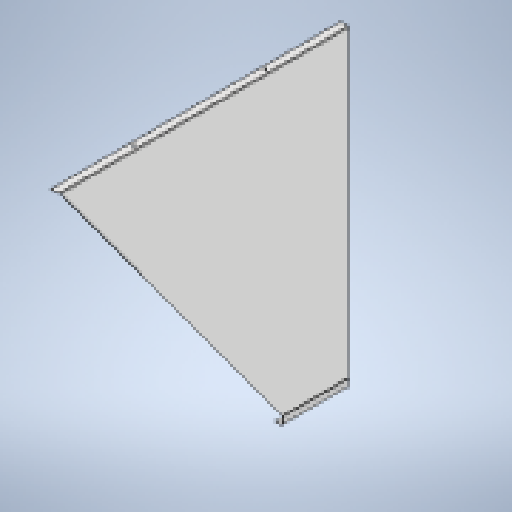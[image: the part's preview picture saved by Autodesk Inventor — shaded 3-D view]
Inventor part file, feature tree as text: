
AUTODESK INVENTOR PART (.ipt)
format: ipt  version: 2025.1 (Build 291241020, 241B)  size: 336,896 bytes
history: native  units: mm
features: sheet_metal_op x9, sketch x8, other x7, extrude x3, mirror x1, pattern_linear x1, projected_geometry x1
ambient origin geometry x8: Origin, YZ Plane, XZ Plane, XY Plane, X Axis, Y Axis, Z Axis, Center Point
bodies: Body1 (feature_tree)
feature tree (30):
  sheet_metal_op  "Contour Flange2"
  extrude  "Extrusion7"  Depth=8.0mm
  extrude  "Extrusion11"  Depth=3.0mm
  other  "A-Side Definition"
  extrude  "Extrusion15"  Depth=3.0mm
  mirror  "Mirror1"
  sheet_metal_op  "Flange3"
  sheet_metal_op  "Flange4"
  pattern_linear  "Rectangular Pattern1"  Count1=174  [1 undecoded]
  sketch  "Sketch1"  dims[d0=1170.0mm d63=8.0mm]
  other  "Plate4"
  sheet_metal_op  "Bend4"
  sheet_metal_op  "Corner4"
  sketch  "Sketch10"  dims[d64=0.0mm d66=3.0mm]
  sketch  "Sketch14"  dims[d67=3.0mm d68=1.5mm]
  sketch  "Sketch20"  dims[d69=6.0mm]
  projected_geometry  "Projected Loop13"
  sketch  "Sketch21"  dims[d70=5.0mm d71=1740.0mm]
  other  "Plate5"
  sheet_metal_op  "Bend5"
  sheet_metal_op  "Corner5"
  sketch  "Sketch22"  dims[d72=5.0mm]
  other  "Plate6"
  sheet_metal_op  "Bend6"
  sheet_metal_op  "Corner6"
  sketch  "Sketch23"  dims[d73=4.0mm]
  sketch  "Sketch24"  dims[d74=12.0mm d75=3.0mm d76=5.0mm d81=10.0mm d82=0.0mm d99=76.5mm d100=0.0mm d101=0.0mm d102=60.0mm d110=3.0mm d111=400.0mm d120=120.0deg d121=175.0mm d122=8.0mm d123=0.0mm d124=850.499815mm d125=50.0mm d126=3.0mm d127=1.5mm d128=6.0mm d129=5.0mm d130=50.0mm d131=30.0deg d132=5.0mm d133=12.0mm d134=3.0mm d135=5.0mm d136=3.0mm d137=1.5mm d138=6.0mm d139=5.0mm d140=45.0mm d141=90.0deg d142=5.0mm d143=12.0mm d144=3.0mm d145=5.0mm d146=14.0mm d147=20.0mm d148=3.0mm d149=0.0mm d150=30.0mm d152=160.0mm d153=16.0mm d154=800.0mm d155=20.0mm d156=3.0mm d157=0.0mm]
  other  "Cut1"
  other  "Cut2"
  other  "Definition1"
note: 1 required parameter value undecoded (feature->parameter linkage not recoverable at this tier; creation-order binding heuristic only, values carry confidence <= 0.55)
